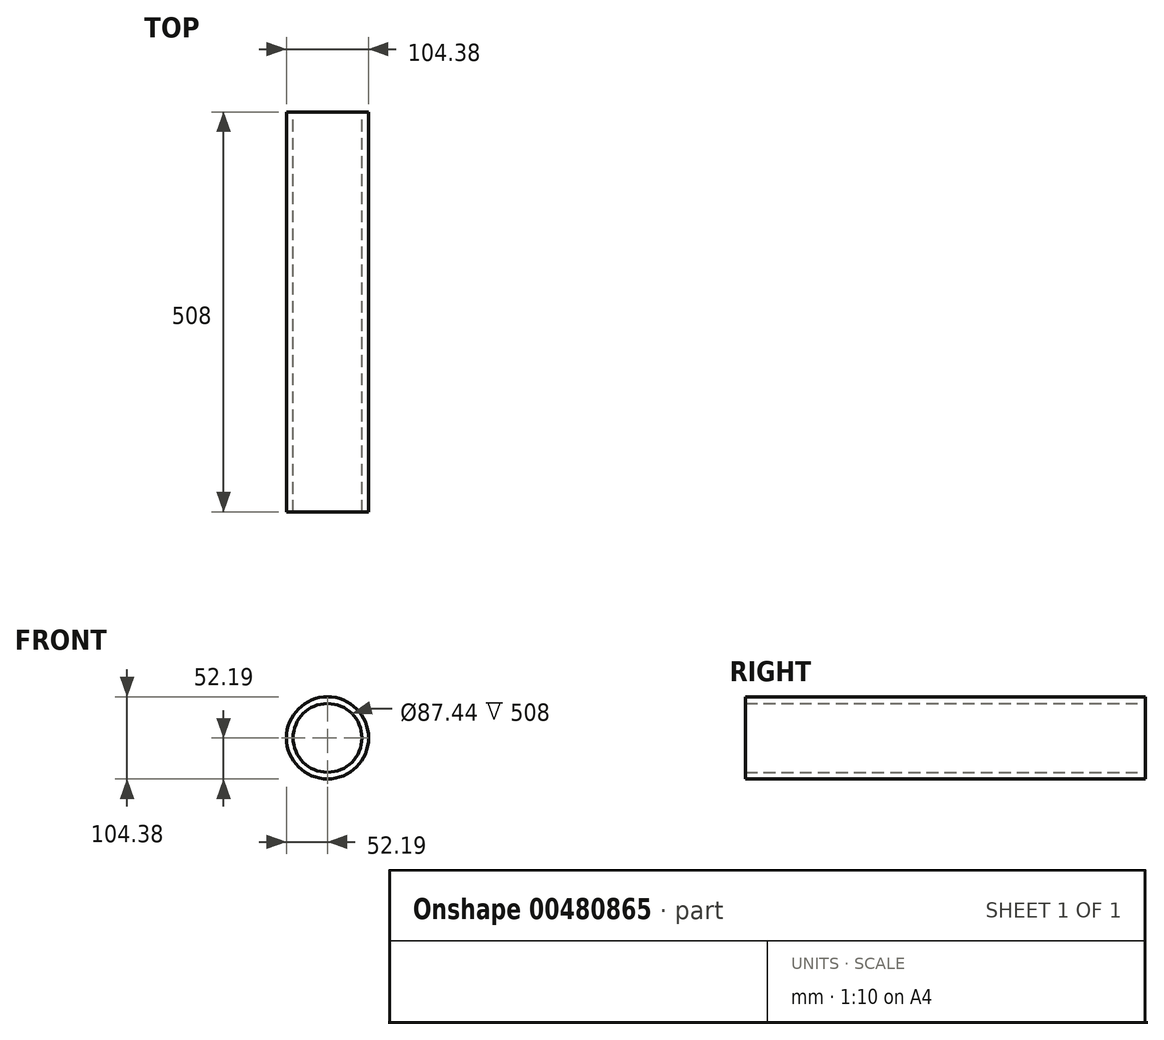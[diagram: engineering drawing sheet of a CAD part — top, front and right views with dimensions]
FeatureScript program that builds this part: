
annotation { "Feature Type Name" : "Feature", "Feature Type Description" : "" }
export const myFeature = defineFeature(function(context is Context, id is Id, definition is map)
    precondition{}
    {
        {
            var Q0;
            Q0=qCreatedBy(makeId("Front.planeOp"),FACE);
            var sketch = newSketch(context, id + "F0", { "sketchPlane" : qUnion([Q0])});
            skCircle(sketch, "E0", {"center": v(0, 0) * mm, "radius": 52.2 * mm});
            skCircle(sketch, "E1", {"center": v(0, 0) * mm, "radius": 43.72 * mm});
            skSolve(sketch);
        }
        {
            var Q0;
            Q0 = qSketchRegion(id + "F0", true);
            var Q1;
            Q1=sQuery(id+"F0.wireOp",EDGE,"E1");
            var Q2;
            Q2=sQuery(id+"F0.wireOp",EDGE,"E0");
            extrude(context, id + "F1", {"entities" : qUnion([Q0]), "surfaceEntities" : qUnion([Q1, Q2]), "depth" : 508 * mm});
        }
    });
